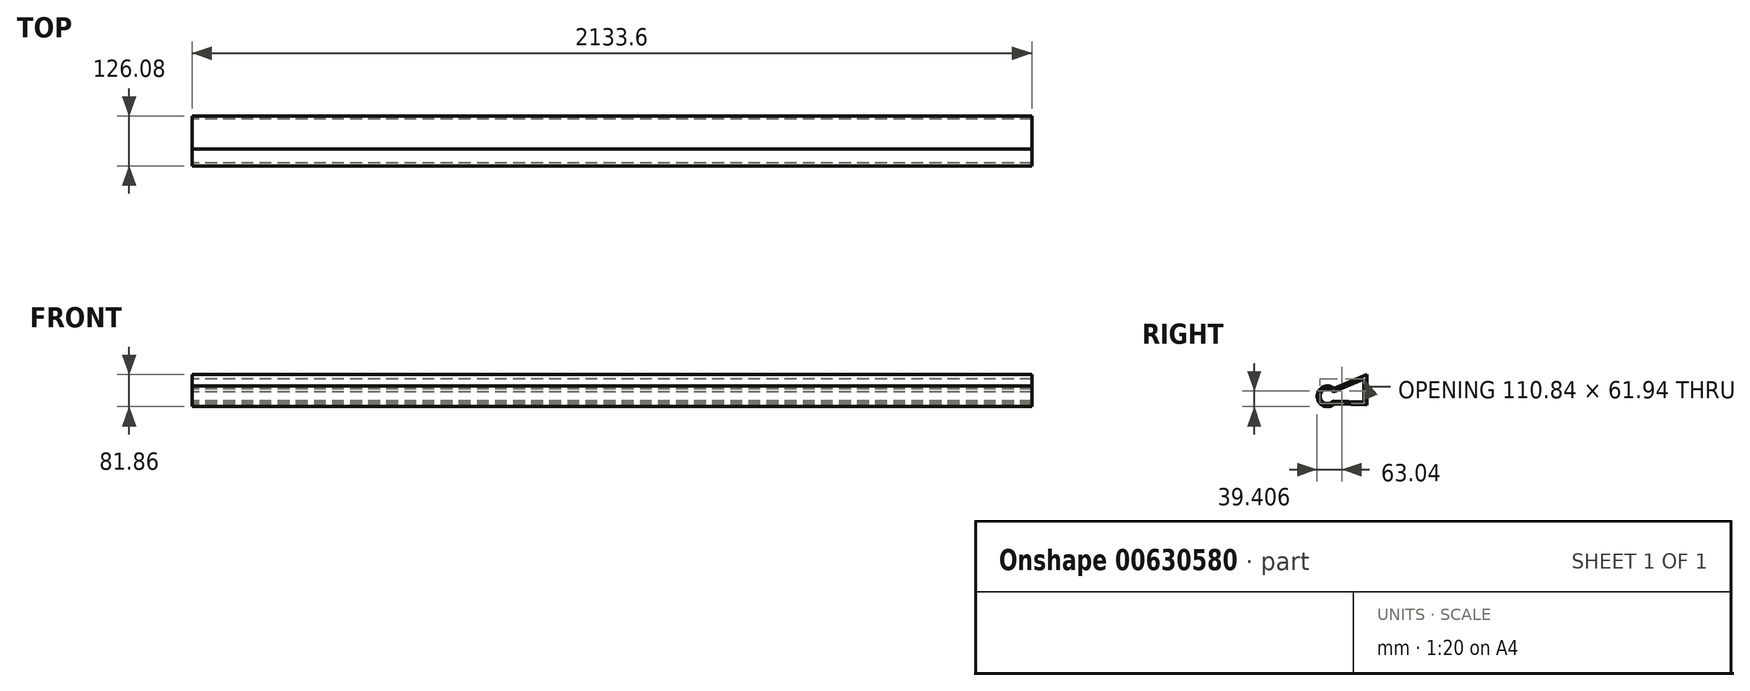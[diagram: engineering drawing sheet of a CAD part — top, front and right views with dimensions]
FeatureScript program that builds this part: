
annotation { "Feature Type Name" : "Feature", "Feature Type Description" : "" }
export const myFeature = defineFeature(function(context is Context, id is Id, definition is map)
    precondition{}
    {
        {
            var Q0;
            Q0=qCreatedBy(makeId("Right.planeOp"),FACE);
            var sketch = newSketch(context, id + "F0", { "sketchPlane" : qUnion([Q0])});
            skCircle(sketch, "E0", {"center": v(0, 0) * mm, "radius": 26.26 * mm});
            skLineSegment(sketch, "E1", {"start": v(16.45, 20.47) * mm, "end": v(99.82, 55.6) * mm});
            skLineSegment(sketch, "E2", {"start": v(99.82, 55.6) * mm, "end": v(99.82, -21.9) * mm});
            skLineSegment(sketch, "E3", {"start": v(99.82, -21.9) * mm, "end": v(18.06, -19.06) * mm});
            skSolve(sketch);
        }
        {
            var Q0;
            Q0 = qSketchRegion(id + "F0", true);
            extrude(context, id + "F1", {"entities" : qUnion([Q0]), "depth" : 2133.6 * mm, "offsetDistance" : 25.4 * mm});
        }
        {
            var Q0;
            Q0=makeQuery(id+"F1.opExtrude","CAP_FACE",FACE,{"disambiguationData":[OSD([sQuery(id+"F0.wireOp",EDGE,"E0"),sQuery(id+"F0.wireOp",EDGE,"E1"),sQuery(id+"F0.wireOp",EDGE,"E2"),sQuery(id+"F0.wireOp",EDGE,"E3")])],"isStart":true});
            var sketch = newSketch(context, id + "F2", { "sketchPlane" : qUnion([Q0])});
            skLineSegment(sketch, "E4.0", {"start": v(-14.7, 11.46) * mm, "end": v(-92.2, 44.12) * mm});
            skArc(sketch, "E4.1", {"start": v(-14.7, 11.46) * mm, "mid": v(18.64, -0.09) * mm, "end": v(-14.8, -11.32) * mm});
            skLineSegment(sketch, "E4.2", {"start": v(-92.2, -14) * mm, "end": v(-14.8, -11.32) * mm});
            skLineSegment(sketch, "E4.3", {"start": v(-92.2, 44.12) * mm, "end": v(-92.2, -14) * mm});
            skSolve(sketch);
        }
        {
            var Q0;
            Q0=makeQuery(id+"F2.imprint","IMPRINT",FACE,{"disambiguationData":[TD([[makeQuery(id+"F2.imprint","IMPRINT",EDGE,{"derivedFrom":sQuery(id+"F2.wireOp",EDGE,"E4.0")}),1.0]])]});
            extrude(context, id + "F3", {"entities" : qUnion([Q0]), "operationType" : NewBodyOperationType.REMOVE, "oppositeDirection" : true, "depth" : 2133.6 * mm, "offsetDistance" : 25.4 * mm});
        }
    });
